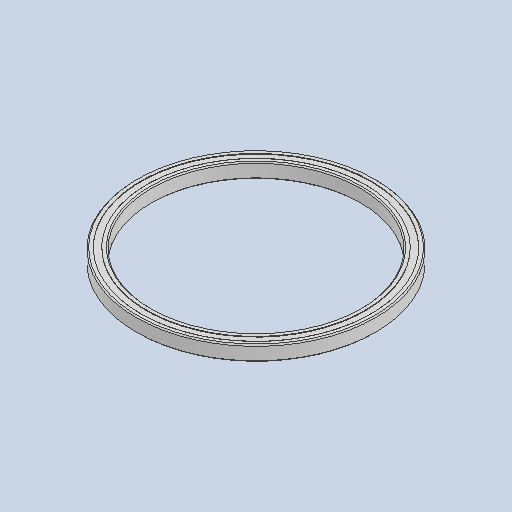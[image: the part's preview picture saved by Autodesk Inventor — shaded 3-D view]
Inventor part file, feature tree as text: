
AUTODESK INVENTOR PART (.ipt)
format: ipt  version: 2022.3 (Build 263350000, 350)  size: 125,952 bytes
history: native  units: in
note: dims shown in document units (in); Inventor stores cm internally (conversion verified against a paired STEP export)
features: revolve x1
ambient origin geometry x8: Origin, YZ Plane, XZ Plane, XY Plane, X Axis, Y Axis, Z Axis, Center Point
bodies: Solid1 (feature_tree)
feature tree (1):
  revolve  "Revolve1"  [1 undecoded]
note: 1 required parameter value undecoded (feature->parameter linkage not recoverable at this tier; creation-order binding heuristic only, values carry confidence <= 0.55)
